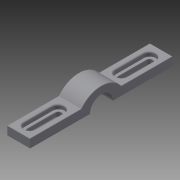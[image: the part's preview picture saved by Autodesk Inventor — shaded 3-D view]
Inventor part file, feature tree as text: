
AUTODESK INVENTOR PART (.ipt)
format: ipt  version: 2015 (Build 190159000, 159)  size: 205,824 bytes
history: native  units: in
note: dims shown in document units (in); Inventor stores cm internally (conversion verified against a paired STEP export)
features: sketch x5, fillet x5, extrude x3, mirror x1
ambient origin geometry x8: Origin, YZ Plane, XZ Plane, XY Plane, X Axis, Y Axis, Z Axis, Center Point
bodies: Solid1 (feature_tree)
feature tree (14):
  sketch  "Sketch1"  dims[d0=0.9843in d1=0.1181in]
  extrude  "Extrusion1"  Depth=0.1181in
  extrude  "Extrusion2"  Depth=0.7087in
  extrude  "Extrusion3"  Depth=0.0787in
  fillet  "Fillet1"  Radius=0.0787in
  fillet  "Fillet2"  Radius=0.1575in
  sketch  "Sketch5"  dims[d18=0.0591in d19=0.0in d20=0.0197in d21=0.0079in d22=0.1575in d23=0.0079in d24=0.0079in d25=0.0079in]
  mirror  "Mirror1"
  fillet  "Fillet3"  Radius=0.1575in
  fillet  "Fillet4"  Radius=0.0591in
  fillet  "Fillet5"  Radius=0.0787in
  sketch  "Sketch2"  dims[d2=0.1575in d5=0.7087in]
  sketch  "Sketch3"  dims[d8=0.315in d9=0.0in d10=0.0787in d11=0.0787in d12=0.1575in d13=0.1575in d14=0.0591in d15=0.0in d16=0.0787in]
  sketch  "Sketch4"  dims[d17=0.0787in]
